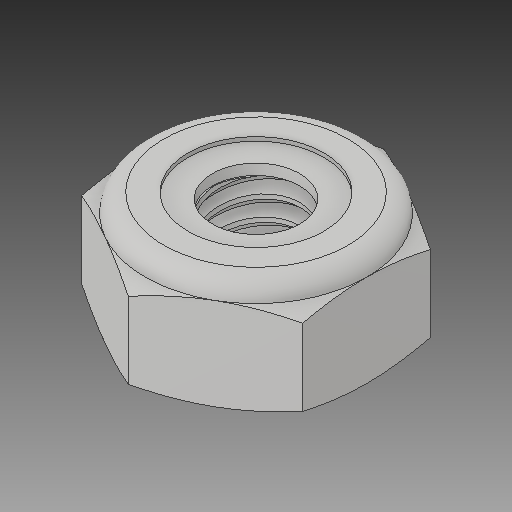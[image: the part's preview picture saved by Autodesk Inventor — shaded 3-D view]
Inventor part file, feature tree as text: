
AUTODESK INVENTOR PART (.ipt)
format: ipt  version: 2018 (Build 220112000, 112)  size: 288,256 bytes
history: native  units: in
note: dims shown in document units (in); Inventor stores cm internally (conversion verified against a paired STEP export)
features: other x1, revolve x1
ambient origin geometry x8: Origin, YZ Plane, XZ Plane, XY Plane, X Axis, Y Axis, Z Axis, Center Point
bodies: Solid1 (feature_tree), Solid2 (feature_tree)
feature tree (2):
  other  "Cut-Revolve4"
  revolve  "Revolve2"  [1 undecoded]
note: 1 required parameter value undecoded (feature->parameter linkage not recoverable at this tier; creation-order binding heuristic only, values carry confidence <= 0.55)
